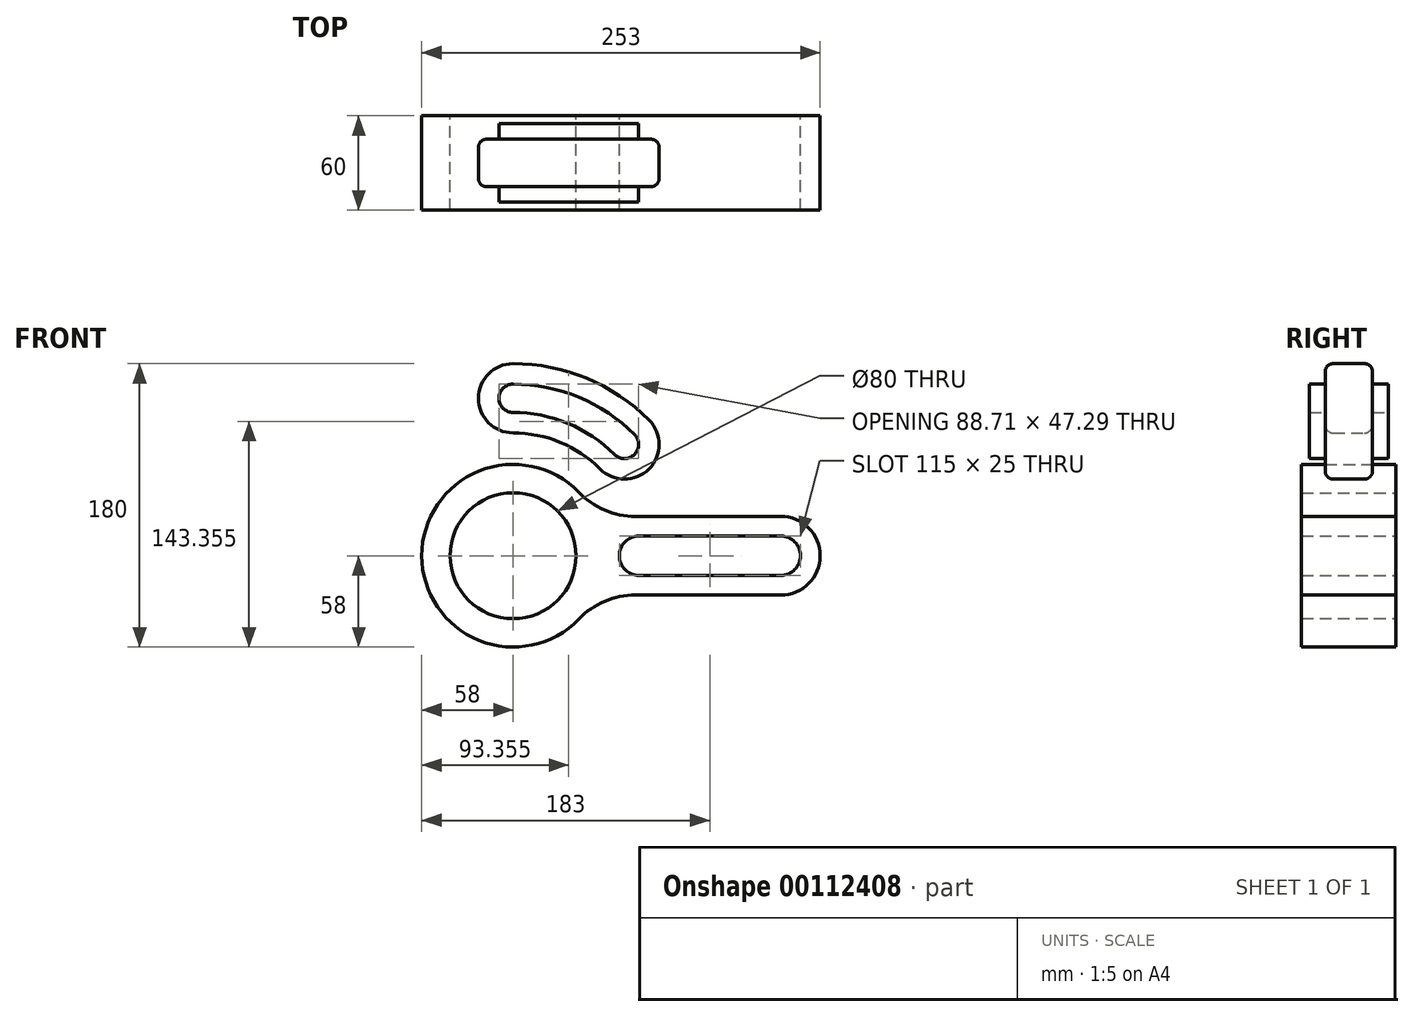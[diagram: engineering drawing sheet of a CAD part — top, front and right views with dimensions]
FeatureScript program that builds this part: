
annotation { "Feature Type Name" : "Feature", "Feature Type Description" : "" }
export const myFeature = defineFeature(function(context is Context, id is Id, definition is map)
    precondition{}
    {
        {
            var Q0;
            Q0=qCreatedBy(makeId("Front.planeOp"),FACE);
            var sketch = newSketch(context, id + "F0", { "sketchPlane" : qUnion([Q0])});
            skArc(sketch, "E0", {"start": v(0, 100) * mm, "mid": v(38.27, 92.39) * mm, "end": v(70.71, 70.71) * mm, "construction": true});
            skArc(sketch, "E1.0.startCap", {"start": v(0, 91) * mm, "mid": v(-9, 100) * mm, "end": v(0, 109) * mm});
            skArc(sketch, "E1.0.endCap", {"start": v(77.07, 77.07) * mm, "mid": v(77.07, 64.35) * mm, "end": v(64.35, 64.35) * mm});
            skArc(sketch, "E1.0.left", {"start": v(0, 109) * mm, "mid": v(41.71, 100.7) * mm, "end": v(77.07, 77.07) * mm});
            skArc(sketch, "E1.0.right", {"start": v(0, 91) * mm, "mid": v(34.82, 84.07) * mm, "end": v(64.35, 64.35) * mm});
            skArc(sketch, "E2.0", {"start": v(0, 78) * mm, "mid": v(29.85, 72.06) * mm, "end": v(55.15, 55.15) * mm});
            skArc(sketch, "E2.1", {"start": v(0, 78) * mm, "mid": v(-22, 100) * mm, "end": v(0, 122) * mm});
            skArc(sketch, "E2.2", {"start": v(0, 122) * mm, "mid": v(46.69, 112.71) * mm, "end": v(86.27, 86.27) * mm});
            skArc(sketch, "E2.3", {"start": v(86.27, 86.27) * mm, "mid": v(86.27, 55.15) * mm, "end": v(55.15, 55.15) * mm});
            skCircle(sketch, "E3", {"center": v(0, 0) * mm, "radius": 40 * mm});
            skLineSegment(sketch, "E4", {"start": v(0, 0) * mm, "end": v(80, 0) * mm, "construction": true});
            skLineSegment(sketch, "E5", {"start": v(80, 0) * mm, "end": v(170, 0) * mm, "construction": true});
            skArc(sketch, "E6.0.startCap", {"start": v(80, -12.5) * mm, "mid": v(67.5, 0) * mm, "end": v(80, 12.5) * mm});
            skArc(sketch, "E6.0.endCap", {"start": v(170, 12.5) * mm, "mid": v(182.5, 0) * mm, "end": v(170, -12.5) * mm});
            skLineSegment(sketch, "E6.0.left", {"start": v(80, 12.5) * mm, "end": v(170, 12.5) * mm});
            skLineSegment(sketch, "E6.0.right", {"start": v(80, -12.5) * mm, "end": v(170, -12.5) * mm});
            skLineSegment(sketch, "E7.0", {"start": v(77.71, 25) * mm, "end": v(170, 25) * mm});
            skLineSegment(sketch, "E7.2", {"start": v(77.71, -25) * mm, "end": v(170, -25) * mm});
            skArc(sketch, "E7.3", {"start": v(170, 25) * mm, "mid": v(195, 0) * mm, "end": v(170, -25) * mm});
            skLineSegment(sketch, "E8", {"start": v(0, 0) * mm, "end": v(70.71, 70.71) * mm, "construction": true});
            skLineSegment(sketch, "E9", {"start": v(186.65, 18.88) * mm, "end": v(69.61, 100.2) * mm});
            skArc(sketch, "E10", {"start": v(41.73, 40.28) * mm, "mid": v(-58, 0) * mm, "end": v(41.73, -40.28) * mm});
            skArc(sketch, "E11", {"start": v(41.73, 40.28) * mm, "mid": v(58.17, 28.98) * mm, "end": v(77.71, 25) * mm});
            skArc(sketch, "E12", {"start": v(41.73, -40.28) * mm, "mid": v(58.17, -28.98) * mm, "end": v(77.71, -25) * mm});
            skArc(sketch, "E13", {"start": v(-23, 53.24) * mm, "mid": v(-11.38, 67.43) * mm, "end": v(-16.2, 85.12) * mm});
            skSolve(sketch);
        }
        {
            var Q0;
            Q0=makeQuery(id+"F0.imprint","IMPRINT",FACE,{"disambiguationData":[TD([[makeQuery(id+"F0.imprint","IMPRINT",EDGE,{"derivedFrom":sQuery(id+"F0.wireOp",EDGE,"E3")}),-1.0]])]});
            extrude(context, id + "F1", {"entities" : qUnion([Q0]), "endBound" : BoundingType.SYMMETRIC, "depth" : 60 * mm});
        }
        {
            var Q0;
            {var subQ6=sQuery(id+"F0.wireOp",EDGE,"E2.0");Q0=makeQuery(id+"F0.imprint","IMPRINT",FACE,{"disambiguationData":[TD([[makeQuery(id+"F0.imprint","IMPRINT",EDGE,{"derivedFrom":subQ6}),-1.0]])]});}
            extrude(context, id + "F2", {"entities" : qUnion([Q0]), "operationType" : NewBodyOperationType.ADD, "endBound" : BoundingType.SYMMETRIC, "depth" : 30 * mm});
        }
        {
            var Q0;
            Q0=makeQuery(id+"F0.imprint","IMPRINT",FACE,{"disambiguationData":[TD([[makeQuery(id+"F0.imprint","IMPRINT",EDGE,{"derivedFrom":sQuery(id+"F0.wireOp",EDGE,"E1.0.startCap")}),1.0]])]});
            extrude(context, id + "F3", {"entities" : qUnion([Q0]), "operationType" : NewBodyOperationType.ADD, "endBound" : BoundingType.SYMMETRIC, "depth" : 50 * mm});
        }
        {
            var Q0;
            Q0=makeQuery(id+"F2.opExtrude","CAP_EDGE",EDGE,{"disambiguationData":[OSD([sQuery(id+"F0.wireOp",EDGE,"E9")])],"isStart":false});
            var Q1;
            Q1=makeQuery(id+"F2.opExtrude","CAP_EDGE",EDGE,{"disambiguationData":[OSD([sQuery(id+"F0.wireOp",EDGE,"E2.3")])],"isStart":false});
            var Q2;
            Q2=makeQuery(id+"F2.opExtrude","CAP_EDGE",EDGE,{"disambiguationData":[OSD([sQuery(id+"F0.wireOp",EDGE,"E7.0")])],"isStart":false});
            var Q3;
            Q3=makeQuery(id+"F2.opExtrude","CAP_EDGE",EDGE,{"disambiguationData":[OSD([sQuery(id+"F0.wireOp",EDGE,"E9")])],"isStart":true});
            var Q4;
            Q4=makeQuery(id+"F2.opExtrude","CAP_EDGE",EDGE,{"disambiguationData":[OSD([sQuery(id+"F0.wireOp",EDGE,"E7.0")])],"isStart":true});
            var Q5;
            Q5=makeQuery(id+"F2.opExtrude","SWEPT_EDGE",EDGE,{"disambiguationData":[OSD([sQuery(id+"F0.wireOp",EDGE,"E10"),sQuery(id+"F0.wireOp",EDGE,"E13")])]});
            var Q6;
            Q6=makeQuery(id+"F2.opExtrude","CAP_EDGE",EDGE,{"disambiguationData":[OSD([sQuery(id+"F0.wireOp",EDGE,"E2.3")])],"isStart":true});
            fillet(context, id + "F4", {"entities" : qUnion([Q0, Q1, Q2, Q3, Q4, Q5, Q6]), "radius" : 5 * mm, "tangentPropagation" : true, "allowEdgeOverflow" : false});
        }
    });
